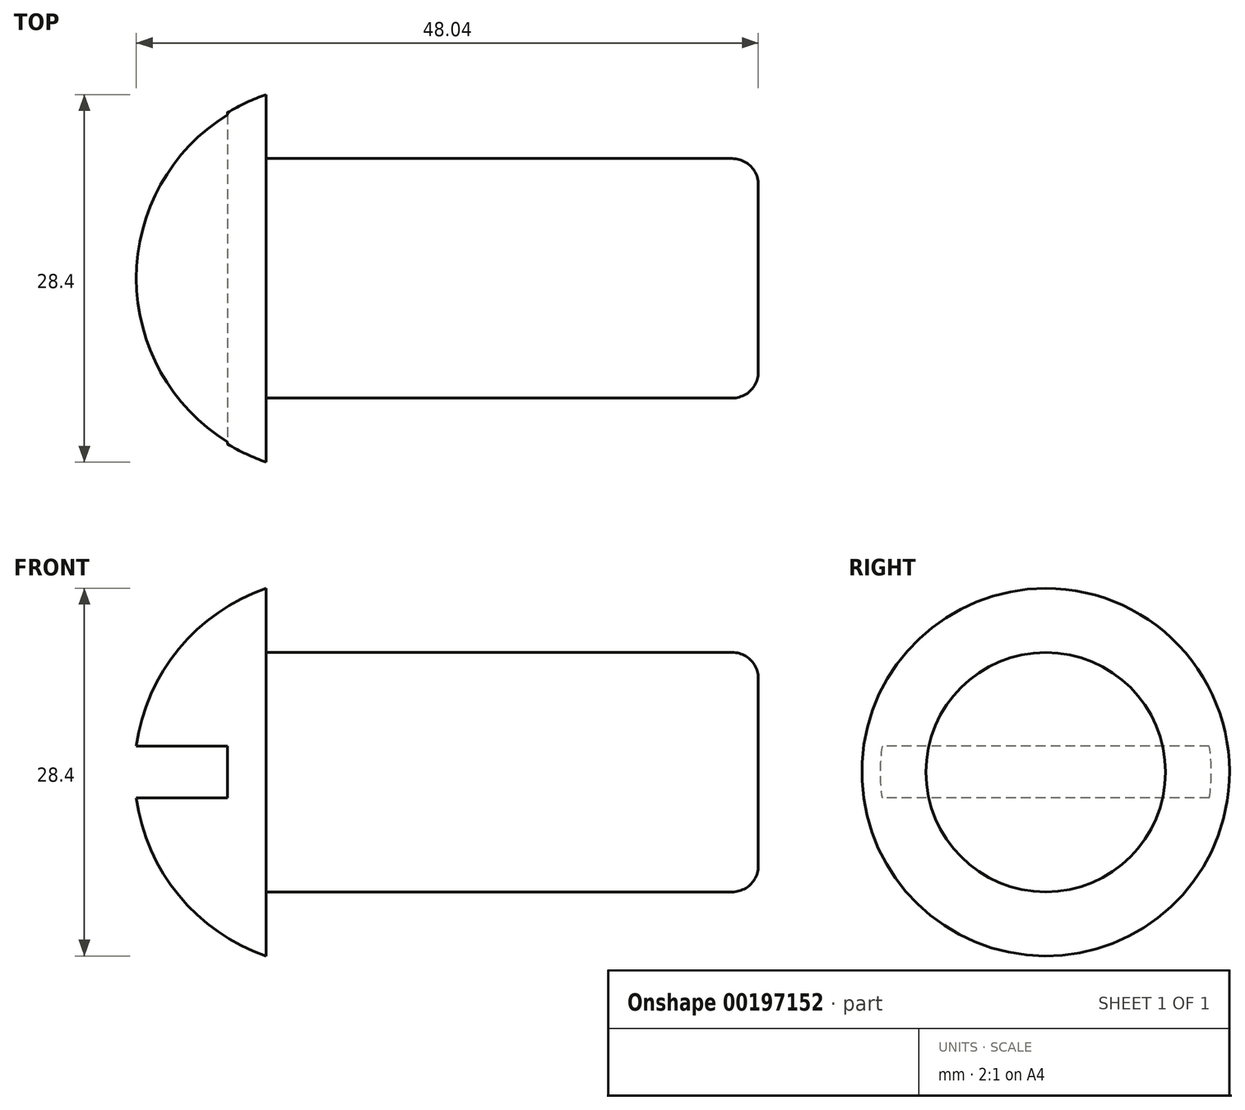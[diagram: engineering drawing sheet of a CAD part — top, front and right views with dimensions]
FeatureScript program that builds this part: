
annotation { "Feature Type Name" : "Feature", "Feature Type Description" : "" }
export const myFeature = defineFeature(function(context is Context, id is Id, definition is map)
    precondition{}
    {
        {
            var Q0;
            Q0=qCreatedBy(makeId("Top.planeOp"),FACE);
            var sketch = newSketch(context, id + "F0", { "sketchPlane" : qUnion([Q0])});
            skLineSegment(sketch, "E0", {"start": v(-43.32, 0) * mm, "end": v(-7.63, 0) * mm, "construction": true});
            skLineSegment(sketch, "E1", {"start": v(22.7, 0) * mm, "end": v(22.7, 9.25) * mm});
            skLineSegment(sketch, "E2", {"start": v(22.7, 9.25) * mm, "end": v(-15.3, 9.25) * mm});
            skLineSegment(sketch, "E3", {"start": v(-15.3, 9.25) * mm, "end": v(-15.3, 14.2) * mm});
            skArc(sketch, "E4", {"start": v(-25.47, 0) * mm, "mid": v(-22.67, 8.73) * mm, "end": v(-15.3, 14.2) * mm});
            skLineSegment(sketch, "E5", {"start": v(-25.47, 0) * mm, "end": v(22.7, 0) * mm});
            skSolve(sketch);
        }
        {
            var Q0;
            Q0=makeQuery(id+"F0.imprint","IMPRINT",FACE,{"disambiguationData":[TD([[makeQuery(id+"F0.imprint","IMPRINT",EDGE,{"derivedFrom":sQuery(id+"F0.wireOp",EDGE,"E1")}),1.0]])]});
            var Q1;
            Q1=sQuery(id+"F0.wireOp",EDGE,"E0");
            revolve(context, id + "F1", {"entities" : qUnion([Q0]), "axis" : qUnion([Q1]), "revolveType" : RevolveType.FULL});
        }
        {
            var Q0;
            Q0=qCreatedBy(makeId("Front.planeOp"),FACE);
            var sketch = newSketch(context, id + "F2", { "sketchPlane" : qUnion([Q0])});
            skLineSegment(sketch, "E6.bottom", {"start": v(-18.3, -2) * mm, "end": v(-25.75, -2) * mm});
            skLineSegment(sketch, "E6.top", {"start": v(-18.3, 2) * mm, "end": v(-25.75, 2) * mm});
            skLineSegment(sketch, "E6.left", {"start": v(-18.3, -2) * mm, "end": v(-18.3, 2) * mm});
            skLineSegment(sketch, "E6.right", {"start": v(-25.75, -2) * mm, "end": v(-25.75, 2) * mm});
            skPoint(sketch, "E6.middle", {"position": v(-22.03, 0) * mm});
            skSolve(sketch);
        }
        {
            var Q0;
            Q0 = qSketchRegion(id + "F2", true);
            extrude(context, id + "F4", {"entities" : qUnion([Q0]), "operationType" : NewBodyOperationType.REMOVE, "endBound" : BoundingType.SYMMETRIC, "oppositeDirection" : true, "depth" : 35.47 * mm});
        }
        {
            var Q0;
            Q0=makeQuery(id+"F1.opRevolve","SWEPT_EDGE",EDGE,{"disambiguationData":[OSD([sQuery(id+"F0.wireOp",EDGE,"E1"),sQuery(id+"F0.wireOp",EDGE,"E2")])]});
            fillet(context, id + "F3", {"entities" : qUnion([Q0]), "radius" : 2 * mm, "tangentPropagation" : true, "allowEdgeOverflow" : false});
        }
    });
